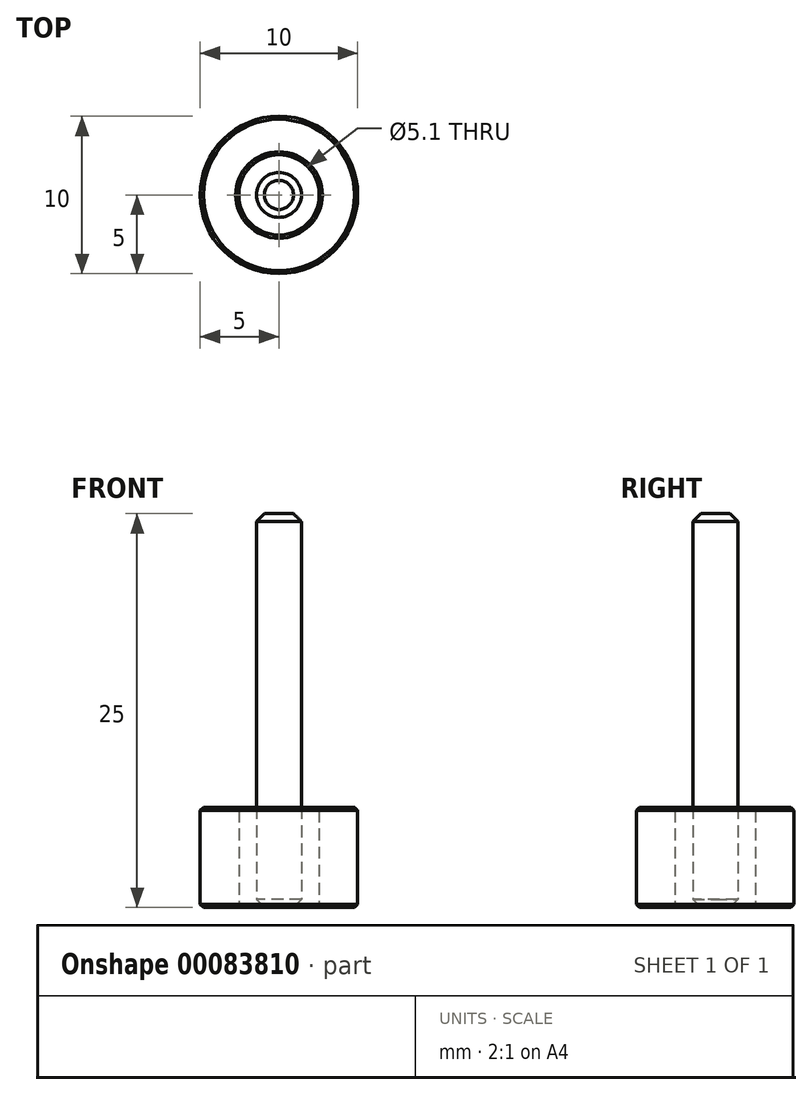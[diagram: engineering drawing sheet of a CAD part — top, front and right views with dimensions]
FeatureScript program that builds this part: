
annotation { "Feature Type Name" : "Feature", "Feature Type Description" : "" }
export const myFeature = defineFeature(function(context is Context, id is Id, definition is map)
    precondition{}
    {
        {
            var Q0;
            Q0=qCreatedBy(makeId("Top.planeOp"),FACE);
            var sketch = newSketch(context, id + "F0", { "sketchPlane" : qUnion([Q0])});
            skCircle(sketch, "E0", {"center": v(0, 0) * mm, "radius": 1.43 * mm});
            skSolve(sketch);
        }
        {
            var Q0;
            Q0 = qSketchRegion(id + "F0", true);
            extrude(context, id + "F6", {"entities" : qUnion([Q0]), "depth" : 25 * mm});
        }
        {
            var Q0;
            Q0=makeQuery(id+"F6.opExtrude","CAP_EDGE",EDGE,{"disambiguationData":[OSD([sQuery(id+"F0.wireOp",EDGE,"E0")])],"isStart":false});
            chamfer(context, id + "F1", {"entities" : qUnion([Q0]), "width" : 0.5 * mm, "tangentPropagation" : true});
        }
        {
            var Q0;
            Q0=makeQuery(id+"F6.opExtrude","CAP_EDGE",EDGE,{"disambiguationData":[OSD([sQuery(id+"F0.wireOp",EDGE,"E0")])],"isStart":true});
            chamfer(context, id + "F2", {"entities" : qUnion([Q0]), "width" : 0.5 * mm, "tangentPropagation" : true});
        }
        {
            var Q0;
            Q0=qCreatedBy(makeId("Top.planeOp"),FACE);
            var sketch = newSketch(context, id + "F3", { "sketchPlane" : qUnion([Q0])});
            skCircle(sketch, "E1", {"center": v(0, 0) * mm, "radius": 2.55 * mm});
            skCircle(sketch, "E2", {"center": v(0, 0) * mm, "radius": 5 * mm});
            skSolve(sketch);
        }
        {
            var Q0;
            Q0 = qSketchRegion(id + "F3", true);
            extrude(context, id + "F4", {"entities" : qUnion([Q0]), "depth" : 25.4 / 4 * mm});
        }
        {
            var Q0;
            Q0=makeQuery(id+"F4.opExtrude","CAP_EDGE",EDGE,{"disambiguationData":[OSD([sQuery(id+"F3.wireOp",EDGE,"E1")])],"isStart":false});
            var Q1;
            Q1=makeQuery(id+"F4.opExtrude","CAP_EDGE",EDGE,{"disambiguationData":[OSD([sQuery(id+"F3.wireOp",EDGE,"E2")])],"isStart":false});
            var Q2;
            Q2=makeQuery(id+"F4.opExtrude","CAP_EDGE",EDGE,{"disambiguationData":[OSD([sQuery(id+"F3.wireOp",EDGE,"E2")])],"isStart":true});
            var Q3;
            Q3=makeQuery(id+"F4.opExtrude","CAP_EDGE",EDGE,{"disambiguationData":[OSD([sQuery(id+"F3.wireOp",EDGE,"E1")])],"isStart":true});
            chamfer(context, id + "F5", {"entities" : qUnion([Q0, Q1, Q2, Q3]), "width" : 0.2 * mm, "tangentPropagation" : true});
        }
    });
